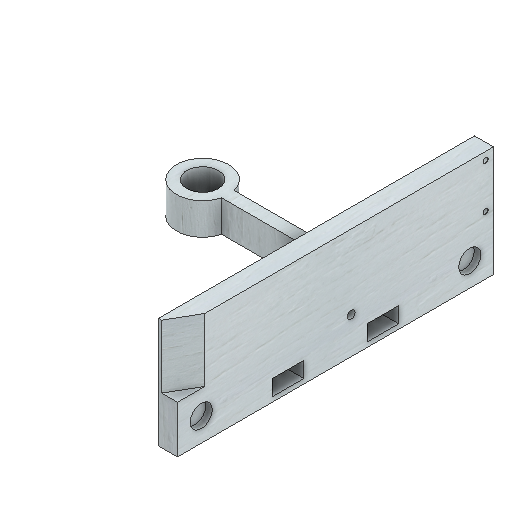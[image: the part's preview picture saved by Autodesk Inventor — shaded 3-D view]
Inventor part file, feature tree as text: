
AUTODESK INVENTOR PART (.ipt)
format: ipt  version: 2022 (Build 260153000, 153)  size: 288,768 bytes
history: native  units: mm
features: other x7, sketch x7, extrude x5, reference x5, hole x3, chamfer x1
ambient origin geometry x8: Origin, YZ Plane, XZ Plane, XY Plane, X Axis, Y Axis, Z Axis, Center Point
bodies: Body1 (feature_tree)
feature tree (28):
  other  "Твердое тело1"
  extrude  "Выдавливание1"  Depth=200.0mm
  extrude  "Выдавливание2"  Depth=30.0mm
  hole  "Отверстие1"  [1 undecoded]
  hole  "Отверстие2"  [1 undecoded]
  chamfer  "Фаска1"  Distance=12.0mm
  extrude  "Выдавливание3"  Depth=12.0mm TaperAngle=0.0deg
  hole  "Отверстие3"  [1 undecoded]
  extrude  "Выдавливание4"  Depth=10.0mm
  extrude  "Выдавливание6"  Depth=20.0mm
  sketch  "Эскиз1"
  sketch  "Эскиз2"
  sketch  "Эскиз4"
  sketch  "Эскиз5"
  sketch  "Эскиз6"
  sketch  "Эскиз7"
  sketch  "Эскиз10"
  reference  "Ссылка2"
  reference  "Ссылка3"
  reference  "Ссылка4"
  reference  "Ссылка5"
  reference  "Ссылка6"
  other  "<userpath>\Documents\Inventor\Файлы Inventor\Сборка всего.iam"
  other  "Сборка всего.iam"
  other  "Задняя стенка:1"
  other  "Механизм подъема:1"
  other  "NEMA17_STEPPER:1"
  other  "Резьбовой винт:1"
note: 3 required parameter values undecoded (feature->parameter linkage not recoverable at this tier; creation-order binding heuristic only, values carry confidence <= 0.55)
